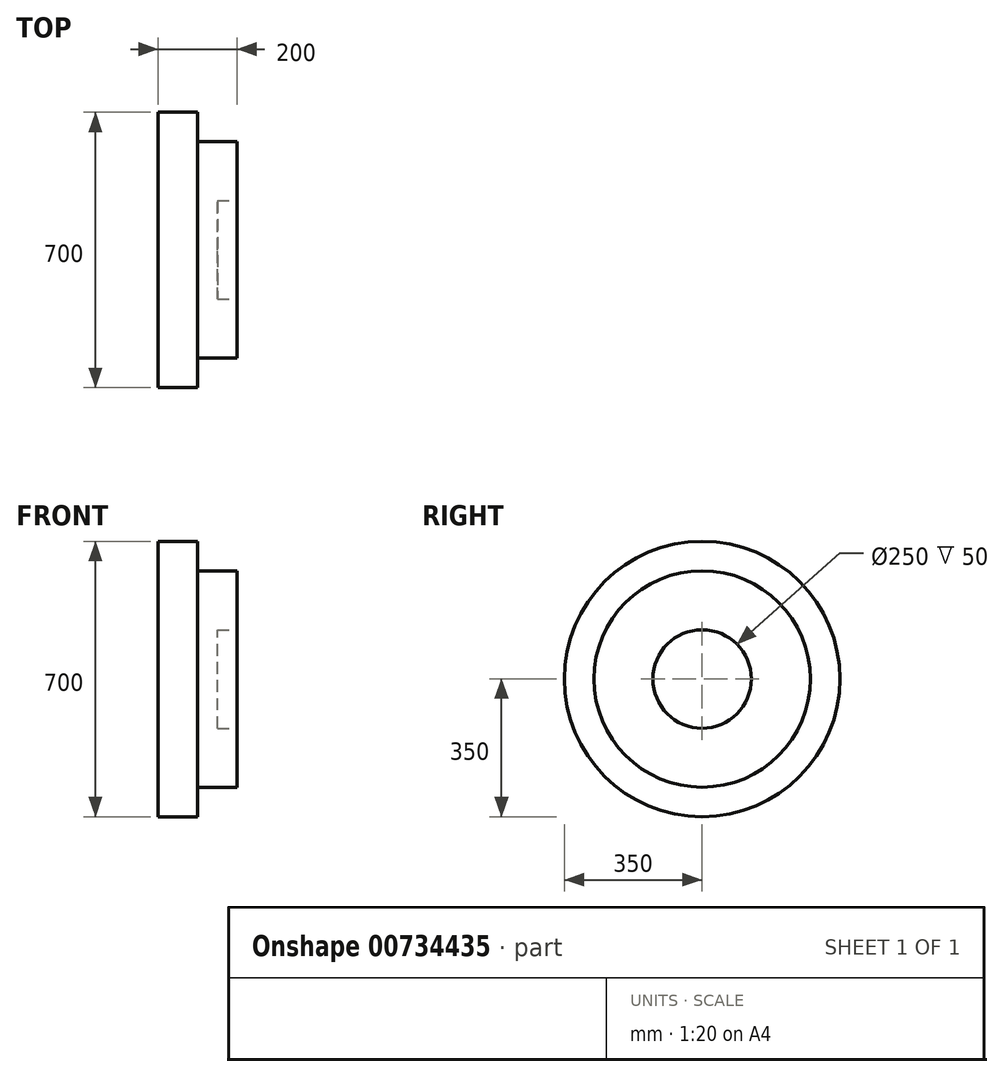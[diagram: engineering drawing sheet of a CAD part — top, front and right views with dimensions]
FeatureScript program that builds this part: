
annotation { "Feature Type Name" : "Feature", "Feature Type Description" : "" }
export const myFeature = defineFeature(function(context is Context, id is Id, definition is map)
    precondition{}
    {
        {
            var Q0;
            Q0=qCreatedBy(makeId("Right.planeOp"),FACE);
            var sketch = newSketch(context, id + "F0", { "sketchPlane" : qUnion([Q0])});
            skCircle(sketch, "E0", {"center": v(0, 0) * mm, "radius": 350 * mm});
            skSolve(sketch);
        }
        {
            var Q0;
            Q0 = qSketchRegion(id + "F0", true);
            extrude(context, id + "F1", {"entities" : qUnion([Q0]), "depth" : 100 * mm, "offsetDistance" : 25 * mm});
        }
        {
            var Q0;
            Q0=makeQuery(id+"F1.opExtrude","CAP_FACE",FACE,{"disambiguationData":[OSD([sQuery(id+"F0.wireOp",EDGE,"E0")])],"isStart":false});
            var sketch = newSketch(context, id + "F2", { "sketchPlane" : qUnion([Q0])});
            skCircle(sketch, "E1", {"center": v(0, 0) * mm, "radius": 275 * mm});
            skSolve(sketch);
        }
        {
            var Q0;
            Q0=makeQuery(id+"F2.imprint","IMPRINT",FACE,{"disambiguationData":[TD([[makeQuery(id+"F2.imprint","IMPRINT",EDGE,{"derivedFrom":sQuery(id+"F2.wireOp",EDGE,"E1")}),1.0]])]});
            var Q1;
            Q1 = qBodyType(qCreatedBy(id + "F2" ,EDGE), BodyType.WIRE);
            var Q2;
            Q2=sQuery(id+"F2.wireOp",EDGE,"E1");
            extrude(context, id + "F3", {"entities" : qUnion([Q0]), "surfaceEntities" : qUnion([Q1, Q2]), "depth" : 100 * mm, "offsetDistance" : 25 * mm});
        }
        {
            var Q0;
            Q0=makeQuery(id+"F3.opExtrude","CAP_FACE",FACE,{"disambiguationData":[OSD([sQuery(id+"F2.wireOp",EDGE,"E1")])],"isStart":false});
            var sketch = newSketch(context, id + "F4", { "sketchPlane" : qUnion([Q0])});
            skCircle(sketch, "E2", {"center": v(0, 0) * mm, "radius": 125 * mm});
            skSolve(sketch);
        }
        {
            var Q0;
            Q0 = qSketchRegion(id + "F4", true);
            extrude(context, id + "F5", {"entities" : qUnion([Q0]), "operationType" : NewBodyOperationType.REMOVE, "oppositeDirection" : true, "depth" : 50 * mm, "offsetDistance" : 25 * mm});
        }
    });
